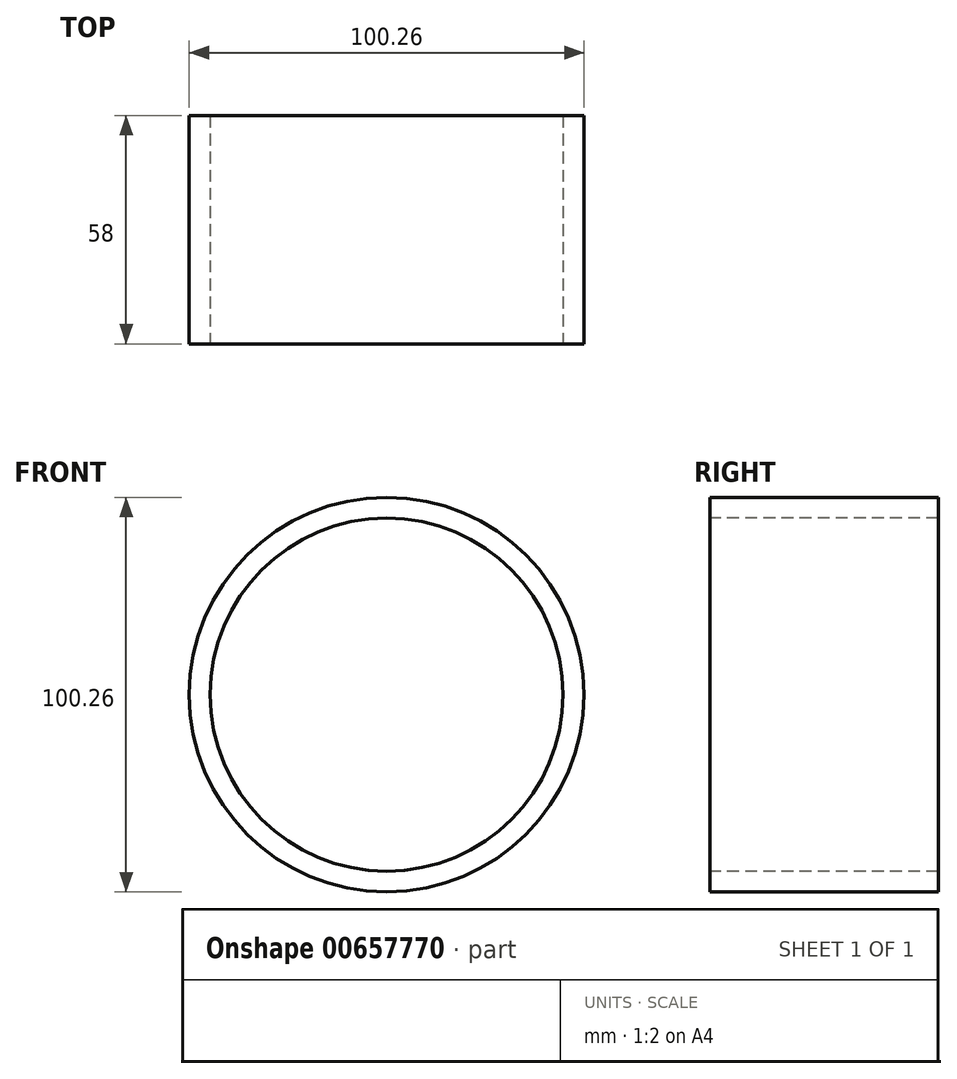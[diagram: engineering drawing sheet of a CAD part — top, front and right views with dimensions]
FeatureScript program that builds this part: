
annotation { "Feature Type Name" : "Feature", "Feature Type Description" : "" }
export const myFeature = defineFeature(function(context is Context, id is Id, definition is map)
    precondition{}
    {
        {
            var Q0;
            Q0=qCreatedBy(makeId("Front.planeOp"),FACE);
            var sketch = newSketch(context, id + "F0", { "sketchPlane" : qUnion([Q0])});
            skCircle(sketch, "E0", {"center": v(0, 0) * mm, "radius": 50.13 * mm});
            skCircle(sketch, "E1", {"center": v(0, 0) * mm, "radius": 44.84 * mm});
            skSolve(sketch);
        }
        {
            var Q0;
            Q0=sQuery(id+"F0.wireOp",EDGE,"E0");
            var Q1;
            Q1=sQuery(id+"F0.wireOp",EDGE,"E1");
            extrude(context, id + "F1", {"bodyType" : ToolBodyType.SURFACE, "surfaceEntities" : qUnion([Q0, Q1]), "depth" : 58 * mm, "offsetDistance" : 25 * mm});
        }
    });
